# Revit family: Outlet-Bath-Caroma Elegance II-Wall1
name_source: partatom
category: Plumbing Fixtures
revit_build: Autodesk Revit 2013 (Build: 20121003_2115(x64)
units: mm (PartAtom-declared; Revit-internal decimal feet)

## types (2) — shared parameters
Assembly Code = C1030210
CW Connection = Yes
CWFU = 4
Connector Radius = 10 mm  [stored 0.0328084 ft]
Default Elevation = 500 mm  [stored 1.64042 ft]
HW Connection = Yes
HWFU = 4
Manufacturer = GWA Bathrooms & Kitchens
Material_ANZRS = Metal-Chrome-Caroma
URL = http://www.caroma.com.au
Vent Connection = No
Waste Connection = No
zero-valued in all types: Cost

## per-type parameters (varying)
| type | Extended | Knee Length | Model | Type Comments |
| Elegance II Bath Outlet 180mm | No | 117 mm  [stored 0.383858 ft] | 631176C | Caroma Elegance II Bath Outlet 180mm |
| Elegance II Bath Outlet Extended 225mm | Yes | 162 mm  [stored 0.531496 ft] | 631177C | Caroma Elegance II Bath Outlet Extended 225mm |

note: [stored X ft] marks values corroborated as IEEE doubles in the binary element streams (Revit-internal decimal feet)

## geometry (parser evidence)
native form markers: Blend x10, Sweep x1
no freeform markers — native parametric forms only
